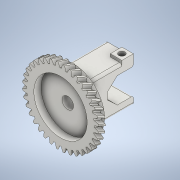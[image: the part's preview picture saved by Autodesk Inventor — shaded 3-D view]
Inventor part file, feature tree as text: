
AUTODESK INVENTOR PART (.ipt)
format: ipt  version: 2022 (Build 260153070, 153G)  size: 762,368 bytes
history: native  units: mm (DEFAULTED — no unit token found)
features: extrude x10, sketch x10, plane x5, other x4, fillet x3, pattern_circular x1, loft x1
ambient origin geometry x8: Origin, YZ Plane, XZ Plane, XY Plane, X Axis, Y Axis, Z Axis, Center Point
bodies: Solid1 (feature_tree)
feature tree (34):
  extrude  "Extrusion1"  Depth=3.0mm TaperAngle=0.0deg
  plane  "Work Plane2"
  plane  "Work Plane8"
  plane  "Work Plane9"
  other  "Spur Gear"
  sketch  "Sketch4"  dims[d41=0.0mm d43=20.0mm]
  extrude  "Extrusion3"  Depth=10.0mm TaperAngle=0.0deg
  fillet  "Fillet1"  Radius=20.0mm
  sketch  "Sketch6"  dims[d49=23.05mm d50=0.15mm d51=0.0mm d52=27.0mm]
  extrude  "Extrusion5"  TaperAngle=0.0deg  [1 undecoded]
  extrude  "Extrusion6"  Depth=20.0mm
  extrude  "Extrusion2"  TaperAngle=0.0deg  [1 undecoded]
  extrude  "Extrusion4"  Depth=0.15mm TaperAngle=0.0deg
  fillet  "Fillet2"  Radius=27.0mm
  sketch  "Sketch7"  dims[d53=5.0mm d54=0.0mm d55=2.5mm d56=0.0mm]
  extrude  "Extrusion7"  Depth=2.5mm TaperAngle=0.0deg
  extrude  "Extrusion8"  Depth=5.0mm
  pattern_circular  "Circular Pattern1"  Count=2  [1 undecoded]
  fillet  "Fillet3"  Radius=12.0mm
  plane  "Work Plane11"
  sketch  "Sketch8"  dims[d57=1.0mm d58=5.0mm d59=20.0mm d60=0.0mm d63=12.0mm]
  extrude  "Extrusion9"  Depth=3.5mm
  extrude  "Extrusion10"  Depth=20.0mm TaperAngle=0.0deg
  plane  "Work Plane12"
  loft  "Loft2"
  sketch  "Sketch1"  dims[d0=32.839078mm d1=3.0mm d2=0.0mm]
  sketch  "Sketch2"  dims[d3=31.777284mm d4=10.0mm d5=0.0mm d16=20.0mm]
  other  "Srf1"
  sketch  "Sketch3"  dims[d17=0.0mm d34=0.872665mm d39=0.0mm]
  sketch  "Sketch5"  dims[d46=20.0mm d47=0.0mm d48=0.0mm]
  sketch  "Sketch9"  dims[d64=18.0mm d65=3.5mm]
  sketch  "Sketch10"  dims[d66=3.5mm d67=20.0mm d68=0.0mm d69=5.0mm d70=0.0mm d71=1.0mm d72=5.0mm d73=5.0mm d74=2.7mm d75=2.5mm d76=2.5mm d77=1.2mm d78=0.0mm d79=3.5mm d80=0.0mm d81=20.0mm d82=360.0deg d84=1.0mm d85=3.75mm d90=3.5mm d91=0.0mm d95=3.0mm d96=4.25mm d97=10.0mm d98=0.0mm d99=0.0mm d100=90.0deg d101=0.0mm d102=90.0deg d108=2.0mm d109=2.0mm d110=0.0mm d111=90.0deg d103=0.5mm d104=0.872665mm d105=0.5mm d106=0.872665mm]
  other  "Edges3"
  other  "Pitch Diameter"
note: 3 required parameter values undecoded (feature->parameter linkage not recoverable at this tier; creation-order binding heuristic only, values carry confidence <= 0.55)
